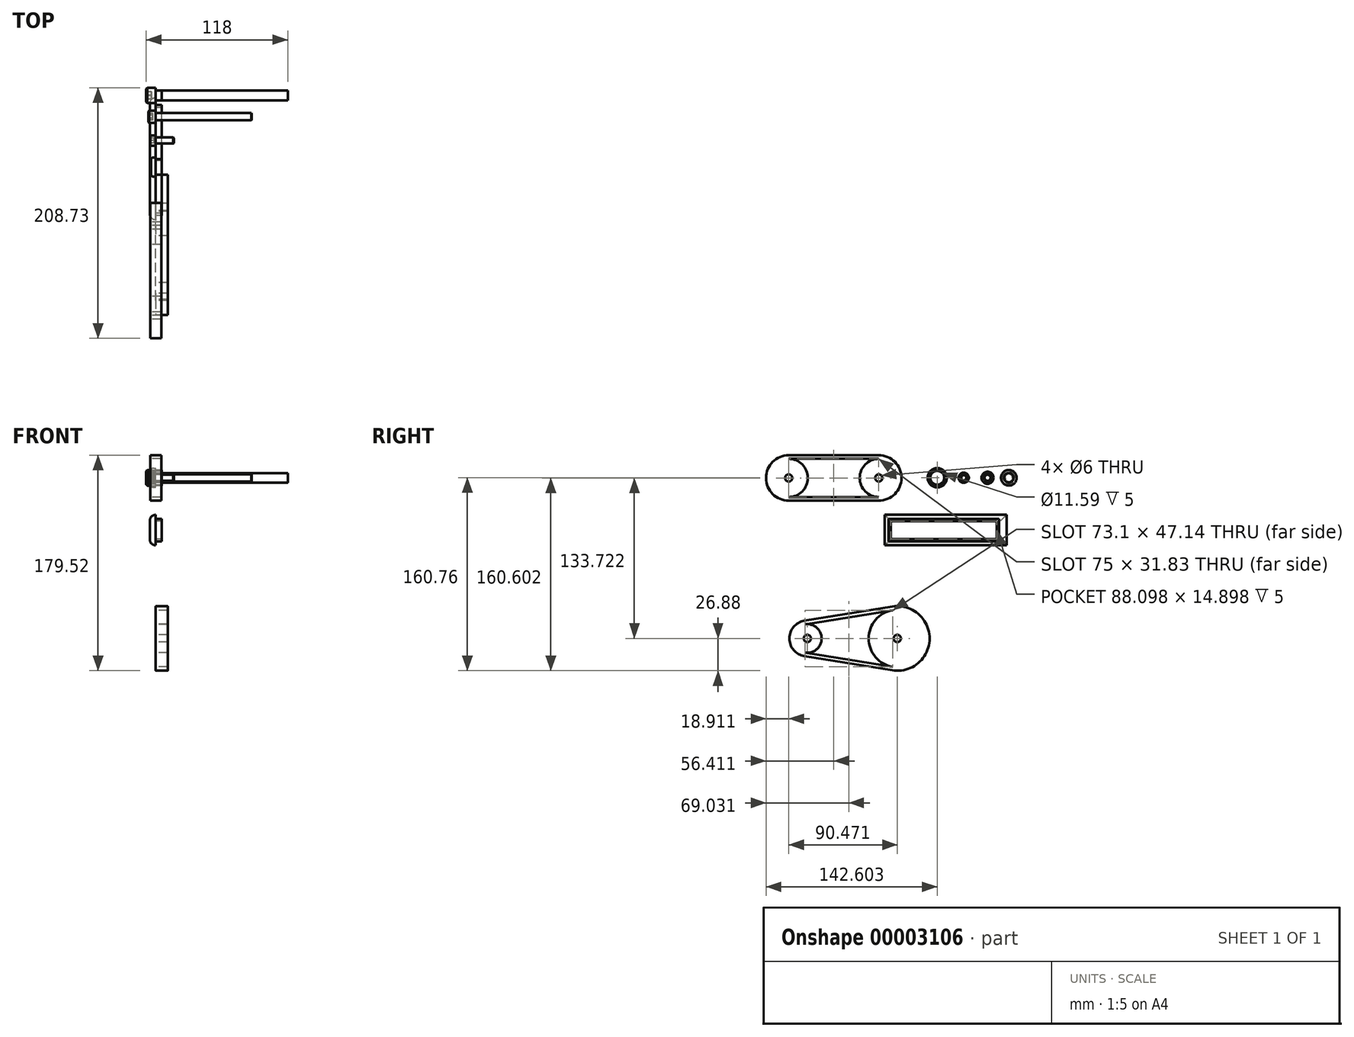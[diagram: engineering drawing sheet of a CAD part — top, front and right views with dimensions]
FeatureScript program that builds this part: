
annotation { "Feature Type Name" : "Feature", "Feature Type Description" : "" }
export const myFeature = defineFeature(function(context is Context, id is Id, definition is map)
    precondition{}
    {
        {
            var Q0;
            Q0=qCreatedBy(makeId("Right.planeOp"),FACE);
            var sketch = newSketch(context, id + "F0", { "sketchPlane" : qUnion([Q0])});
            skCircle(sketch, "E0", {"center": v(-17.3, 0) * mm, "radius": 6.5 * mm});
            skCircle(sketch, "E1", {"center": v(-17.3, 0) * mm, "radius": 4 * mm});
            skSolve(sketch);
        }
        {
            var Q0;
            Q0=makeQuery(id+"F0.imprint","IMPRINT",FACE,{"disambiguationData":[TD([[makeQuery(id+"F0.imprint","IMPRINT",EDGE,{"derivedFrom":sQuery(id+"F0.wireOp",EDGE,"E0")}),1.0]])]});
            var Q1;
            Q1=makeQuery(id+"F0.imprint","IMPRINT",FACE,{"disambiguationData":[TD([[makeQuery(id+"F0.imprint","IMPRINT",EDGE,{"derivedFrom":sQuery(id+"F0.wireOp",EDGE,"E1")}),1.0]])]});
            extrude(context, id + "F1", {"entities" : qUnion([Q0, Q1]), "oppositeDirection" : true, "depth" : 8 * mm});
        }
        {
            var Q0;
            Q0=makeQuery(id+"F0.imprint","IMPRINT",FACE,{"disambiguationData":[TD([[makeQuery(id+"F0.imprint","IMPRINT",EDGE,{"derivedFrom":sQuery(id+"F0.wireOp",EDGE,"E1")}),1.0]])]});
            extrude(context, id + "F2", {"entities" : qUnion([Q0]), "operationType" : NewBodyOperationType.ADD, "depth" : 5 * mm});
        }
        {
            var Q0;
            Q0=makeQuery(id+"F1.opExtrude","CAP_FACE",FACE,{"disambiguationData":[OSD([sQuery(id+"F0.wireOp",EDGE,"E0")])],"isStart":false});
            var sketch = newSketch(context, id + "F3", { "sketchPlane" : qUnion([Q0])});
            skCircle(sketch, "E2.cCircle", {"center": v(17.3, 0) * mm, "radius": 3.46 * mm, "construction": true});
            skLineSegment(sketch, "E2.0", {"start": v(17.69, 3.44) * mm, "end": v(20.47, 1.38) * mm});
            skLineSegment(sketch, "E2.1", {"start": v(20.47, 1.38) * mm, "end": v(20.08, -2.06) * mm});
            skLineSegment(sketch, "E2.2", {"start": v(20.08, -2.06) * mm, "end": v(16.9, -3.44) * mm});
            skLineSegment(sketch, "E2.3", {"start": v(16.9, -3.44) * mm, "end": v(14.12, -1.38) * mm});
            skLineSegment(sketch, "E2.4", {"start": v(14.12, -1.38) * mm, "end": v(14.5, 2.06) * mm});
            skLineSegment(sketch, "E2.5", {"start": v(14.5, 2.06) * mm, "end": v(17.69, 3.44) * mm});
            skSolve(sketch);
        }
        {
            var Q0;
            Q0=makeQuery(id+"F3.imprint","IMPRINT",FACE,{"disambiguationData":[TD([[makeQuery(id+"F3.imprint","IMPRINT",EDGE,{"derivedFrom":sQuery(id+"F3.wireOp",EDGE,"E2.0")}),-1.0]])]});
            extrude(context, id + "F4", {"entities" : qUnion([Q0]), "operationType" : NewBodyOperationType.REMOVE, "oppositeDirection" : true, "depth" : 4.3 * mm});
        }
        {
            var Q0;
            Q0=makeQuery(id+"F1.opExtrude","CAP_EDGE",EDGE,{"disambiguationData":[OSD([sQuery(id+"F0.wireOp",EDGE,"E0")])],"isStart":false});
            chamfer(context, id + "F5", {"entities" : qUnion([Q0]), "width" : 1 * mm, "tangentPropagation" : true});
        }
        {
            var Q0;
            Q0=makeQuery(id+"F2.opExtrude","CAP_FACE",FACE,{"disambiguationData":[OSD([sQuery(id+"F0.wireOp",EDGE,"E1")])],"isStart":false});
            extrude(context, id + "F6", {"entities" : qUnion([Q0]), "depth" : 105 * mm});
        }
        {
            var Q0;
            Q0=makeQuery(id+"F6.opExtrude","CAP_FACE",FACE,{"disambiguationData":[OSD([sQuery(id+"F0.wireOp",EDGE,"E1")])],"isStart":false});
            chamfer(context, id + "F7", {"entities" : qUnion([Q0]), "width" : .1 * mm, "tangentPropagation" : true});
        }
        {
            var Q0;
            Q0=qCreatedBy(makeId("Right.planeOp"),FACE);
            var sketch = newSketch(context, id + "F8", { "sketchPlane" : qUnion([Q0])});
            skCircle(sketch, "E3", {"center": v(-35, 0) * mm, "radius": 5 * mm});
            skSolve(sketch);
        }
        {
            var Q0;
            Q0 = qSketchRegion(id + "F8", true);
            extrude(context, id + "F9", {"entities" : qUnion([Q0]), "oppositeDirection" : true, "depth" : 6 * mm});
        }
        {
            var Q0;
            Q0=makeQuery(id+"F9.opExtrude","CAP_FACE",FACE,{"disambiguationData":[OSD([sQuery(id+"F8.wireOp",EDGE,"E3")])],"isStart":true});
            var sketch = newSketch(context, id + "F10", { "sketchPlane" : qUnion([Q0])});
            skCircle(sketch, "E4", {"center": v(-35, 0) * mm, "radius": 3 * mm});
            skSolve(sketch);
        }
        {
            var Q0;
            Q0 = qSketchRegion(id + "F10", true);
            var Q1;
            Q1=makeQuery(id+"F10.imprint","IMPRINT",FACE,{"disambiguationData":[TD([[makeQuery(id+"F10.imprint","IMPRINT",EDGE,{"derivedFrom":sQuery(id+"F10.wireOp",EDGE,"E4")}),1.0]])]});
            extrude(context, id + "F11", {"entities" : qUnion([Q0, Q1]), "operationType" : NewBodyOperationType.ADD, "depth" : 80 * mm});
        }
        {
            var Q0;
            Q0=makeQuery(id+"F9.opExtrude","CAP_FACE",FACE,{"disambiguationData":[OSD([sQuery(id+"F8.wireOp",EDGE,"E3")])],"isStart":false});
            var sketch = newSketch(context, id + "F12", { "sketchPlane" : qUnion([Q0])});
            skCircle(sketch, "E5.cCircle", {"center": v(35, 0) * mm, "radius": 2.5 * mm, "construction": true});
            skLineSegment(sketch, "E5.0", {"start": v(33.22, -2.27) * mm, "end": v(32.14, 0.4) * mm});
            skLineSegment(sketch, "E5.1", {"start": v(32.14, 0.4) * mm, "end": v(33.92, 2.68) * mm});
            skLineSegment(sketch, "E5.2", {"start": v(33.92, 2.68) * mm, "end": v(36.78, 2.27) * mm});
            skLineSegment(sketch, "E5.3", {"start": v(36.78, 2.27) * mm, "end": v(37.86, -0.4) * mm});
            skLineSegment(sketch, "E5.4", {"start": v(37.86, -0.4) * mm, "end": v(36.08, -2.68) * mm});
            skLineSegment(sketch, "E5.5", {"start": v(36.08, -2.68) * mm, "end": v(33.22, -2.27) * mm});
            skPoint(sketch, "E5.0.midPoint", {"position": v(32.68, -0.94) * mm});
            skSolve(sketch);
        }
        {
            var Q0;
            Q0=makeQuery(id+"F12.imprint","IMPRINT",FACE,{"disambiguationData":[TD([[makeQuery(id+"F12.imprint","IMPRINT",EDGE,{"derivedFrom":sQuery(id+"F12.wireOp",EDGE,"E5.0")}),-1.0]])]});
            extrude(context, id + "F13", {"entities" : qUnion([Q0]), "operationType" : NewBodyOperationType.REMOVE, "oppositeDirection" : true, "depth" : 3.3 * mm});
        }
        {
            var Q0;
            Q0=makeQuery(id+"F9.opExtrude","CAP_EDGE",EDGE,{"disambiguationData":[OSD([sQuery(id+"F8.wireOp",EDGE,"E3")])],"isStart":false});
            var Q1;
            Q1=makeQuery(id+"F11.opExtrude","CAP_EDGE",EDGE,{"disambiguationData":[OSD([sQuery(id+"F10.wireOp",EDGE,"E4")])],"isStart":false});
            chamfer(context, id + "F14", {"entities" : qUnion([Q0, Q1]), "width" : .5 * mm, "tangentPropagation" : true});
        }
        {
            var Q0;
            Q0=qCreatedBy(makeId("Right.planeOp"),FACE);
            var sketch = newSketch(context, id + "F15", { "sketchPlane" : qUnion([Q0])});
            skCircle(sketch, "E6", {"center": v(-76.92, 0) * mm, "radius": 6.5 * mm});
            skCircle(sketch, "E7", {"center": v(-76.92, 0) * mm, "radius": 8 * mm});
            skSolve(sketch);
        }
        {
            var Q0;
            Q0=makeQuery(id+"F15.imprint","IMPRINT",FACE,{"disambiguationData":[TD([[makeQuery(id+"F15.imprint","IMPRINT",EDGE,{"derivedFrom":sQuery(id+"F15.wireOp",EDGE,"E6")}),1.0]])]});
            var Q1;
            Q1=makeQuery(id+"F15.imprint","IMPRINT",FACE,{"disambiguationData":[TD([[makeQuery(id+"F15.imprint","IMPRINT",EDGE,{"derivedFrom":sQuery(id+"F15.wireOp",EDGE,"E6")}),-1.0]])]});
            extrude(context, id + "F16", {"entities" : qUnion([Q0, Q1]), "oppositeDirection" : true, "depth" : 4 * mm});
        }
        {
            var Q0;
            Q0=makeQuery(id+"F15.imprint","IMPRINT",FACE,{"disambiguationData":[TD([[makeQuery(id+"F15.imprint","IMPRINT",EDGE,{"derivedFrom":sQuery(id+"F15.wireOp",EDGE,"E6")}),1.0]])]});
            extrude(context, id + "F17", {"entities" : qUnion([Q0]), "operationType" : NewBodyOperationType.ADD, "depth" : 5 * mm});
        }
        {
            var Q0;
            Q0=makeQuery(id+"F16.opExtrude","CAP_EDGE",EDGE,{"disambiguationData":[OSD([sQuery(id+"F15.wireOp",EDGE,"E7")])],"isStart":false});
            fillet(context, id + "F18", {"entities" : qUnion([Q0]), "radius" : 2 * mm, "tangentPropagation" : true, "allowEdgeOverflow" : false});
        }
        {
            var Q0;
            Q0=makeQuery(id+"F17.opExtrude","CAP_FACE",FACE,{"disambiguationData":[OSD([sQuery(id+"F15.wireOp",EDGE,"E6")])],"isStart":false});
            var sketch = newSketch(context, id + "F19", { "sketchPlane" : qUnion([Q0])});
            skCircle(sketch, "E8", {"center": v(-76.92, 0) * mm, "radius": 5.8 * mm});
            skSolve(sketch);
        }
        {
            var Q0;
            Q0=makeQuery(id+"F19.imprint","IMPRINT",FACE,{"disambiguationData":[TD([[makeQuery(id+"F19.imprint","IMPRINT",EDGE,{"derivedFrom":sQuery(id+"F19.wireOp",EDGE,"E8")}),1.0]])]});
            extrude(context, id + "F20", {"entities" : qUnion([Q0]), "operationType" : NewBodyOperationType.REMOVE, "oppositeDirection" : true, "depth" : 5 * mm});
        }
        {
            var Q0;
            Q0=qCreatedBy(makeId("Right.planeOp"),FACE);
            var sketch = newSketch(context, id + "F21", { "sketchPlane" : qUnion([Q0])});
            skArc(sketch, "E9", {"start": v(-125.6, -16.07) * mm, "mid": v(-109.7, -0.16) * mm, "end": v(-125.6, 15.76) * mm});
            skArc(sketch, "E10", {"start": v(-200.6, 15.76) * mm, "mid": v(-216.52, -0.16) * mm, "end": v(-200.6, -16.07) * mm});
            skLineSegment(sketch, "E11", {"start": v(-200.6, 15.76) * mm, "end": v(-187.76, 15.76) * mm});
            skLineSegment(sketch, "E12", {"start": v(-200.6, -16.07) * mm, "end": v(-125.6, -16.07) * mm});
            skLineSegment(sketch, "E13.0", {"start": v(-200.6, 18.76) * mm, "end": v(-125.6, 18.76) * mm});
            skArc(sketch, "E13.1", {"start": v(-200.6, 18.76) * mm, "mid": v(-219.52, -0.16) * mm, "end": v(-200.6, -19.07) * mm});
            skLineSegment(sketch, "E13.2", {"start": v(-200.6, -19.07) * mm, "end": v(-125.6, -19.07) * mm});
            skArc(sketch, "E13.3", {"start": v(-125.6, -19.07) * mm, "mid": v(-106.7, -0.16) * mm, "end": v(-125.6, 18.76) * mm});
            skLineSegment(sketch, "E14.trimOffspring", {"start": v(-187.76, 15.76) * mm, "end": v(-182.76, 15.76) * mm});
            skLineSegment(sketch, "E15.trimOffspring", {"start": v(-182.76, 15.76) * mm, "end": v(-125.6, 15.76) * mm});
            skCircle(sketch, "E16", {"center": v(-200.6, -0.16) * mm, "radius": 15.91 * mm});
            skCircle(sketch, "E17", {"center": v(-200.6, -0.16) * mm, "radius": 3 * mm});
            skCircle(sketch, "E18", {"center": v(-125.6, -0.16) * mm, "radius": 3 * mm});
            skCircle(sketch, "E19", {"center": v(-125.6, -0.16) * mm, "radius": 15.91 * mm});
            skLineSegment(sketch, "E20", {"start": v(-200.6, -0.16) * mm, "end": v(-125.6, -0.16) * mm, "construction": true});
            skSolve(sketch);
        }
        {
            var Q0;
            Q0 = qSketchRegion(id + "F21", true);
            var Q1;
            Q1=makeQuery(id+"F21.imprint","IMPRINT",FACE,{"disambiguationData":[TD([[makeQuery(id+"F21.imprint","IMPRINT",EDGE,{"derivedFrom":sQuery(id+"F21.wireOp",EDGE,"E17")}),-1.0]])]});
            var Q2;
            Q2=makeQuery(id+"F21.imprint","IMPRINT",FACE,{"disambiguationData":[TD([[makeQuery(id+"F21.imprint","IMPRINT",EDGE,{"derivedFrom":sQuery(id+"F21.wireOp",EDGE,"E18")}),-1.0]])]});
            extrude(context, id + "F22", {"entities" : qUnion([Q0, Q1, Q2]), "depth" : 9 * mm, "symmetric" : true});
        }
        {
            var Q0;
            Q0=qCreatedBy(makeId("Right.planeOp"),FACE);
            var sketch = newSketch(context, id + "F23", { "sketchPlane" : qUnion([Q0])});
            skCircle(sketch, "E21", {"center": v(-185.14, -133.88) * mm, "radius": 3 * mm});
            skCircle(sketch, "E22", {"center": v(-110.14, -133.88) * mm, "radius": 3 * mm});
            skLineSegment(sketch, "E23", {"start": v(-187.04, -122.1) * mm, "end": v(-113.94, -110.3) * mm});
            skLineSegment(sketch, "E24", {"start": v(-187.04, -145.66) * mm, "end": v(-113.94, -157.45) * mm});
            skLineSegment(sketch, "E25", {"start": v(-185.14, -133.88) * mm, "end": v(-110.14, -133.88) * mm, "construction": true});
            skLineSegment(sketch, "E26", {"start": v(-175.15, -108.64) * mm, "end": v(-138.53, -108.64) * mm, "construction": true});
            skArc(sketch, "E27", {"start": v(-187.04, -122.1) * mm, "mid": v(-197.07, -133.88) * mm, "end": v(-187.04, -145.66) * mm});
            skArc(sketch, "E28", {"start": v(-187.04, -145.66) * mm, "mid": v(-173.2, -133.88) * mm, "end": v(-187.04, -122.1) * mm});
            skArc(sketch, "E29", {"start": v(-113.94, -110.3) * mm, "mid": v(-134.01, -133.88) * mm, "end": v(-113.94, -157.45) * mm});
            skArc(sketch, "E30", {"start": v(-113.94, -157.45) * mm, "mid": v(-86.26, -133.88) * mm, "end": v(-113.94, -110.3) * mm});
            skArc(sketch, "E31.0", {"start": v(-187.52, -119.14) * mm, "mid": v(-200.07, -133.88) * mm, "end": v(-187.52, -148.62) * mm});
            skLineSegment(sketch, "E31.1", {"start": v(-187.52, -119.14) * mm, "end": v(-114.42, -107.35) * mm});
            skArc(sketch, "E31.2", {"start": v(-114.42, -160.41) * mm, "mid": v(-83.26, -133.88) * mm, "end": v(-114.42, -107.35) * mm});
            skLineSegment(sketch, "E31.3", {"start": v(-187.52, -148.62) * mm, "end": v(-114.42, -160.41) * mm});
            skSolve(sketch);
        }
        {
            var Q0;
            Q0=makeQuery(id+"F23.imprint","IMPRINT",FACE,{"disambiguationData":[TD([[makeQuery(id+"F23.imprint","IMPRINT",EDGE,{"derivedFrom":sQuery(id+"F23.wireOp",EDGE,"E21")}),-1.0]])]});
            var Q1;
            Q1=makeQuery(id+"F23.imprint","IMPRINT",FACE,{"disambiguationData":[TD([[makeQuery(id+"F23.imprint","IMPRINT",EDGE,{"derivedFrom":sQuery(id+"F23.wireOp",EDGE,"E23")}),1.0]])]});
            var Q2;
            Q2=makeQuery(id+"F23.imprint","IMPRINT",FACE,{"disambiguationData":[TD([[makeQuery(id+"F23.imprint","IMPRINT",EDGE,{"derivedFrom":sQuery(id+"F23.wireOp",EDGE,"E22")}),-1.0]])]});
            extrude(context, id + "F24", {"entities" : qUnion([Q0, Q1, Q2]), "depth" : 10 * mm});
        }
        {
            var Q0;
            Q0=qCreatedBy(makeId("Right.planeOp"),FACE);
            var sketch = newSketch(context, id + "F25", { "sketchPlane" : qUnion([Q0])});
            skCircle(sketch, "E32", {"center": v(-54.85, 0) * mm, "radius": 2.5 * mm});
            skCircle(sketch, "E33", {"center": v(-54.85, 0) * mm, "radius": 4.25 * mm});
            skSolve(sketch);
        }
        {
            var Q0;
            Q0=makeQuery(id+"F25.imprint","IMPRINT",FACE,{"disambiguationData":[TD([[makeQuery(id+"F25.imprint","IMPRINT",EDGE,{"derivedFrom":sQuery(id+"F25.wireOp",EDGE,"E32")}),1.0]])]});
            var Q1;
            Q1=makeQuery(id+"F25.imprint","IMPRINT",FACE,{"disambiguationData":[TD([[makeQuery(id+"F25.imprint","IMPRINT",EDGE,{"derivedFrom":sQuery(id+"F25.wireOp",EDGE,"E32")}),-1.0]])]});
            extrude(context, id + "F26", {"entities" : qUnion([Q0, Q1]), "oppositeDirection" : true, "depth" : 5 * mm});
        }
        {
            var Q0;
            Q0=makeQuery(id+"F25.imprint","IMPRINT",FACE,{"disambiguationData":[TD([[makeQuery(id+"F25.imprint","IMPRINT",EDGE,{"derivedFrom":sQuery(id+"F25.wireOp",EDGE,"E32")}),1.0]])]});
            extrude(context, id + "F27", {"entities" : qUnion([Q0]), "operationType" : NewBodyOperationType.ADD, "depth" : 15 * mm});
        }
        {
            var Q0;
            Q0=makeQuery(id+"F26.opExtrude","CAP_FACE",FACE,{"disambiguationData":[OSD([sQuery(id+"F25.wireOp",EDGE,"E33")])],"isStart":false});
            var sketch = newSketch(context, id + "F28", { "sketchPlane" : qUnion([Q0])});
            skCircle(sketch, "E34.cCircle", {"center": v(54.85, 0) * mm, "radius": 2 * mm, "construction": true});
            skLineSegment(sketch, "E34.0", {"start": v(54.88, 2.3) * mm, "end": v(56.86, 1.13) * mm});
            skLineSegment(sketch, "E34.1", {"start": v(56.86, 1.13) * mm, "end": v(56.83, -1.18) * mm});
            skLineSegment(sketch, "E34.2", {"start": v(56.83, -1.18) * mm, "end": v(54.82, -2.3) * mm});
            skLineSegment(sketch, "E34.3", {"start": v(54.82, -2.3) * mm, "end": v(52.83, -1.13) * mm});
            skLineSegment(sketch, "E34.4", {"start": v(52.83, -1.13) * mm, "end": v(52.86, 1.18) * mm});
            skLineSegment(sketch, "E34.5", {"start": v(52.86, 1.18) * mm, "end": v(54.88, 2.3) * mm});
            skPoint(sketch, "E34.0.midPoint", {"position": v(55.87, 1.72) * mm});
            skSolve(sketch);
        }
        {
            var Q0;
            Q0 = qSketchRegion(id + "F28", true);
            var Q1;
            Q1=makeQuery(id+"F28.imprint","IMPRINT",FACE,{"disambiguationData":[TD([[makeQuery(id+"F28.imprint","IMPRINT",EDGE,{"derivedFrom":sQuery(id+"F28.wireOp",EDGE,"E34.0")}),-1.0]])]});
            extrude(context, id + "F29", {"entities" : qUnion([Q0, Q1]), "operationType" : NewBodyOperationType.REMOVE, "oppositeDirection" : true, "depth" : 3.5 * mm});
        }
        {
            var Q0;
            Q0=makeQuery(id+"F26.opExtrude","CAP_EDGE",EDGE,{"disambiguationData":[OSD([sQuery(id+"F25.wireOp",EDGE,"E33")])],"isStart":false});
            var Q1;
            Q1=makeQuery(id+"F27.opExtrude","CAP_EDGE",EDGE,{"disambiguationData":[OSD([sQuery(id+"F25.wireOp",EDGE,"E32")])],"isStart":false});
            chamfer(context, id + "F30", {"entities" : qUnion([Q0, Q1]), "width" : .4 * mm, "tangentPropagation" : true});
        }
        {
            var Q0;
            Q0=qCreatedBy(makeId("Right.planeOp"),FACE);
            var sketch = newSketch(context, id + "F31", { "sketchPlane" : qUnion([Q0])});
            skLineSegment(sketch, "E35.bottom", {"start": v(-117.46, -34.12) * mm, "end": v(-25.36, -34.12) * mm});
            skLineSegment(sketch, "E35.top", {"start": v(-117.46, -53.02) * mm, "end": v(-25.36, -53.02) * mm});
            skLineSegment(sketch, "E35.left", {"start": v(-117.46, -34.12) * mm, "end": v(-117.46, -53.02) * mm});
            skLineSegment(sketch, "E35.right", {"start": v(-25.36, -34.12) * mm, "end": v(-25.36, -53.02) * mm});
            skLineSegment(sketch, "E36.bottom", {"start": v(-120.71, -30.87) * mm, "end": v(-19.11, -30.87) * mm});
            skLineSegment(sketch, "E36.top", {"start": v(-120.71, -56.27) * mm, "end": v(-19.11, -56.27) * mm});
            skLineSegment(sketch, "E36.left", {"start": v(-120.71, -30.87) * mm, "end": v(-120.71, -56.27) * mm});
            skLineSegment(sketch, "E36.right", {"start": v(-19.11, -30.87) * mm, "end": v(-19.11, -56.27) * mm});
            skLineSegment(sketch, "E37.0", {"start": v(-115.46, -36.12) * mm, "end": v(-27.36, -36.12) * mm});
            skLineSegment(sketch, "E37.1", {"start": v(-115.46, -36.12) * mm, "end": v(-115.46, -51.02) * mm});
            skLineSegment(sketch, "E37.2", {"start": v(-115.46, -51.02) * mm, "end": v(-27.36, -51.02) * mm});
            skLineSegment(sketch, "E37.3", {"start": v(-27.36, -36.12) * mm, "end": v(-27.36, -51.02) * mm});
            skSolve(sketch);
        }
        {
            var Q0;
            Q0 = qSketchRegion(id + "F31", true);
            var Q1;
            Q1=makeQuery(id+"F31.imprint","IMPRINT",FACE,{"disambiguationData":[TD([[makeQuery(id+"F31.imprint","IMPRINT",EDGE,{"derivedFrom":sQuery(id+"F31.wireOp",EDGE,"E35.bottom")}),-1.0]])]});
            var Q2;
            Q2=makeQuery(id+"F31.imprint","IMPRINT",FACE,{"disambiguationData":[TD([[makeQuery(id+"F31.imprint","IMPRINT",EDGE,{"derivedFrom":sQuery(id+"F31.wireOp",EDGE,"E37.0")}),-1.0]])]});
            extrude(context, id + "F32", {"entities" : qUnion([Q0, Q1, Q2]), "oppositeDirection" : true, "depth" : 5 * mm});
        }
        {
            var Q0;
            Q0=makeQuery(id+"F31.imprint","IMPRINT",FACE,{"disambiguationData":[TD([[makeQuery(id+"F31.imprint","IMPRINT",EDGE,{"derivedFrom":sQuery(id+"F31.wireOp",EDGE,"E35.bottom")}),-1.0]])]});
            extrude(context, id + "F33", {"entities" : qUnion([Q0]), "operationType" : NewBodyOperationType.ADD, "depth" : 5 * mm});
        }
        {
            var Q0;
            Q0=makeQuery(id+"F32.opExtrude","CAP_EDGE",EDGE,{"disambiguationData":[OSD([sQuery(id+"F31.wireOp",EDGE,"E36.right")])],"isStart":false});
            var Q1;
            Q1=makeQuery(id+"F32.opExtrude","CAP_EDGE",EDGE,{"disambiguationData":[OSD([sQuery(id+"F31.wireOp",EDGE,"E36.top")])],"isStart":false});
            var Q2;
            Q2=makeQuery(id+"F32.opExtrude","CAP_EDGE",EDGE,{"disambiguationData":[OSD([sQuery(id+"F31.wireOp",EDGE,"E36.left")])],"isStart":false});
            var Q3;
            Q3=makeQuery(id+"F32.opExtrude","CAP_EDGE",EDGE,{"disambiguationData":[OSD([sQuery(id+"F31.wireOp",EDGE,"E36.bottom")])],"isStart":false});
            fillet(context, id + "F34", {"entities" : qUnion([Q0, Q1, Q2, Q3]), "radius" : 5 * mm, "tangentPropagation" : true, "allowEdgeOverflow" : false});
        }
    });
